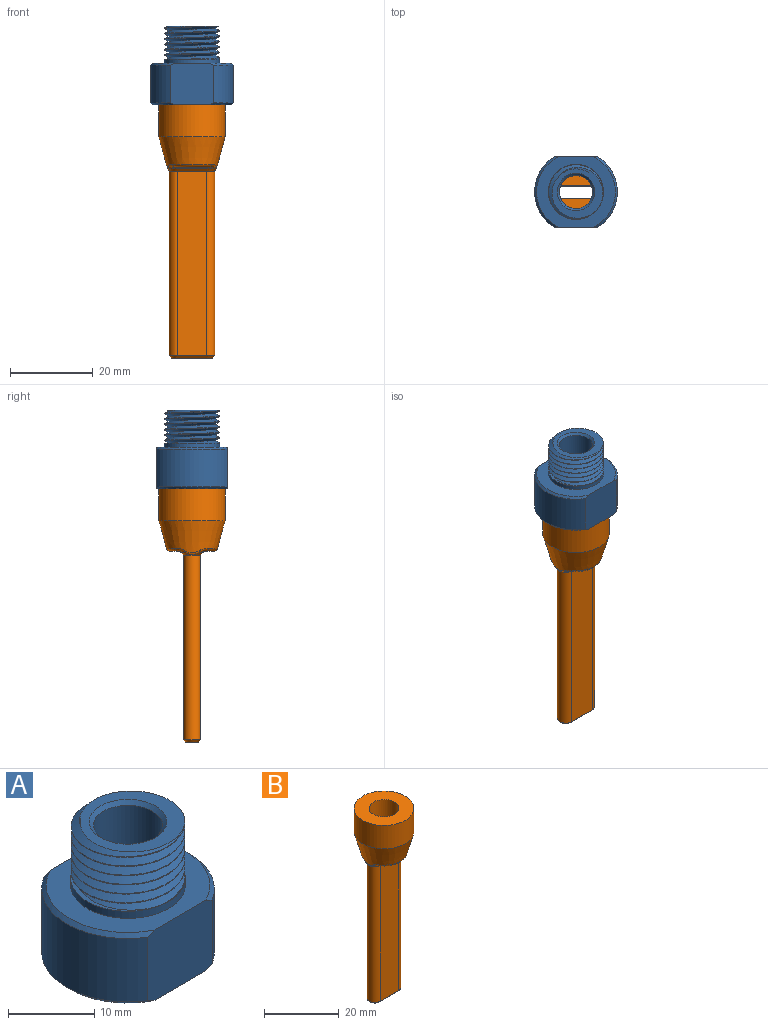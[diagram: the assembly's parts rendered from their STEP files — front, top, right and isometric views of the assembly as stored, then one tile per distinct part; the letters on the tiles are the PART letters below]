
ASSEMBLY  parts=2 mates=1
PART A: 21 faces, bbox 20x17.9x19.8 mm
  f0: plane 0.34x0.29mm, normal (0,1,0), area 0mm2, adj f11,f12,f13
  f1: cylinder r=6.58mm len=13.17mm, axis (0,0,1), area 25.1mm2, adj f6,f10,f11,f12,f14
  f2: cylinder r=10mm len=17mm, axis (0,0,1), area 182.9mm2, adj f7,f8,f17,f19
  f3: cylinder r=10mm len=17mm, axis (0,0,1), area 182.9mm2, adj f7,f8,f16,f18
  f4: plane 19x17mm, normal (0,0,1), area 133.2mm2, adj f7,f8,f15,f18,f19
  f5: plane 19x17mm, normal (0,0,-1), area 221.8mm2, adj f7,f8,f9,f16,f17
  f6: plane 12.25x12.24mm, normal (0,0,1), area 53.8mm2, adj f1,f11,f12,f20
  f7: plane 10.57x10.04mm, normal (0,-1,0), area 104.4mm2, adj f2,f3,f4,f5,f16,f17,f18,f19
  f8: plane 10.57x10.04mm, normal (0,1,0), area 104.4mm2, adj f2,f3,f4,f5,f16,f17,f18,f19
  f9: cylinder r=4mm len=18.5mm, axis (0,0,1), area 465mm2, adj f5,f20
  f10: plane 0.48x0.28mm, normal (0,1,0), area 0.1mm2, adj f1,f12,f14
  f11: bspline ~15.21x13.17mm, area 285.1mm2, adj f0,f1,f6,f12,f13,f14
  f12: bspline ~15.21x13.17mm, area 281.4mm2, adj f0,f1,f6,f10,f11,f13,f14
  f13: cylinder r=5.84mm len=10.05mm, axis (0,0,-1), area 3.1mm2, adj f0,f11,f12,f14
  f14: plane 13.33x13.33mm, normal (0,0,1), area 18mm2, adj f1,f10,f11,f12,f13,f15
  f15: cylinder r=6.65mm len=13.3mm, axis (0,0,-1), area 41.8mm2, adj f4,f14
  f16: cone r=10mm half-angle=45deg, axis (0,0,1), area 14.6mm2, adj f3,f5,f7,f8
  f17: cone r=10mm half-angle=45deg, axis (0,0,1), area 14.6mm2, adj f2,f5,f7,f8
  f18: cone r=9.5mm half-angle=45deg, axis (0,0,-1), area 14.6mm2, adj f3,f4,f7,f8
  f19: cone r=9.5mm half-angle=45deg, axis (0,0,-1), area 14.6mm2, adj f2,f4,f7,f8
  f20: cone r=4mm half-angle=45deg, axis (0,0,1), area 18.9mm2, adj f6,f9
PART B: 40 faces, bbox 16x16x61 mm
  f0: cone r=8mm half-angle=15.2deg, axis (0,0,1), area 314.7mm2, adj f5,f27,f30,f31,f34,f35,f37,f38
  f1: plane 7.43x2.52mm, normal (0,0,1), area 13.4mm2, adj f7,f18,f20,f21
  f2: plane 7.43x2.52mm, normal (0,0,1), area 13.4mm2, adj f7,f18,f19,f20
  f3: plane 8x1.86mm, normal (0,0,-1), area 10mm2, adj f28,f32,f35,f36
  f4: plane 8x1.86mm, normal (0,0,-1), area 10mm2, adj f26,f29,f33,f34
  f5: cylinder r=8mm len=16mm, axis (0,0,1), area 384.5mm2, adj f0,f6
  f6: plane 16x16mm, normal (0,0,1), area 150.8mm2, adj f5,f7
  f7: cylinder r=4mm len=14mm, axis (0,0,1), area 351.9mm2, adj f1,f2,f6,f16,f17
  f8: plane 44.5x7mm, normal (0,1,0), area 311.5mm2, adj f9,f11,f13,f23
  f9: cylinder r=2mm len=44.5mm, axis (0,0,1), area 279.6mm2, adj f8,f10,f12,f22
  f10: plane 44.5x7mm, normal (0,-1,0), area 311.5mm2, adj f9,f11,f14,f24
  f11: cylinder r=2mm len=44.5mm, axis (0,0,1), area 279.6mm2, adj f8,f10,f15,f25
  f12: cone r=2mm half-angle=45deg, axis (0,0,1), area 5.1mm2, adj f9,f13,f14,f26,f27,f28
  f13: plane 7x0.71mm, normal (0,0.71,-0.71), area 7mm2, adj f8,f12,f15,f29
  f14: plane 7x0.71mm, normal (0,-0.71,-0.71), area 7mm2, adj f10,f12,f15,f32
  f15: cone r=3mm half-angle=45deg, axis (0,0,1), area 5.1mm2, adj f11,f13,f14,f33,f36,f39
  f16: plane 2.97x1.29mm, normal (0,0,-1), area 2.3mm2, adj f7,f18
  f17: plane 2.97x1.29mm, normal (0,0,-1), area 2.3mm2, adj f7,f20
  f18: cylinder r=1.5mm len=47mm, axis (0,0,-1), area 221.5mm2, adj f1,f2,f16,f19,f21,f25
  f19: plane 47x7mm, normal (0,-1,0), area 329mm2, adj f2,f18,f20,f23
  f20: cylinder r=1.5mm len=47mm, axis (0,0,-1), area 221.5mm2, adj f1,f2,f17,f19,f21,f22
  f21: plane 47x7mm, normal (0,1,0), area 329mm2, adj f1,f18,f20,f24
  f22: cone r=1.5mm half-angle=45deg, axis (0,0,1), area 3.9mm2, adj f9,f20,f23,f24
  f23: plane 7x0.5mm, normal (0,0.71,-0.71), area 4.9mm2, adj f8,f19,f22,f25
  f24: plane 7x0.5mm, normal (0,-0.71,-0.71), area 4.9mm2, adj f10,f21,f22,f25
  f25: cone r=2mm half-angle=45deg, axis (0,0,1), area 3.9mm2, adj f11,f18,f23,f24
  f26: torus R=3.41mm, axis (0,0,1), area 1mm2, adj f4,f12,f29,f30
  f27: bspline ~4.85x1.33mm, area 2.4mm2, adj f0,f12,f30,f31
  f28: torus R=3.41mm, axis (0,0,1), area 1mm2, adj f3,f12,f31,f32
  f29: cylinder r=1mm len=7mm, axis (1,0,0), area 5.5mm2, adj f4,f13,f26,f33
  f30: bspline ~3.03x2.15mm, area 2.2mm2, adj f0,f26,f27,f34
  f31: bspline ~3.07x2.22mm, area 2.2mm2, adj f0,f27,f28,f35
  f32: cylinder r=1mm len=7mm, axis (1,0,0), area 5.5mm2, adj f3,f14,f28,f36
  f33: torus R=3.41mm, axis (0,0,1), area 1mm2, adj f4,f15,f29,f37
  f34: torus R=5.24mm, axis (0,0,1), area 13.2mm2, adj f0,f4,f30,f37
  f35: torus R=5.24mm, axis (0,0,1), area 13.2mm2, adj f0,f3,f31,f38
  f36: torus R=3.41mm, axis (0,0,1), area 1mm2, adj f3,f15,f32,f38
  f37: bspline ~3.07x2.22mm, area 2.2mm2, adj f0,f33,f34,f39
  f38: bspline ~3.03x2.15mm, area 2.2mm2, adj f0,f35,f36,f39
  f39: bspline ~4.85x1.33mm, area 2.4mm2, adj f0,f15,f37,f38
PLACE A t=(0.11,10.77,-96.06)mm
PLACE B t=(0.11,10.77,-59.57)mm
MATE fastened A.f1 <-> B.f0  axis (0,0,1) through (0.11,10.77,-54.47)mm
